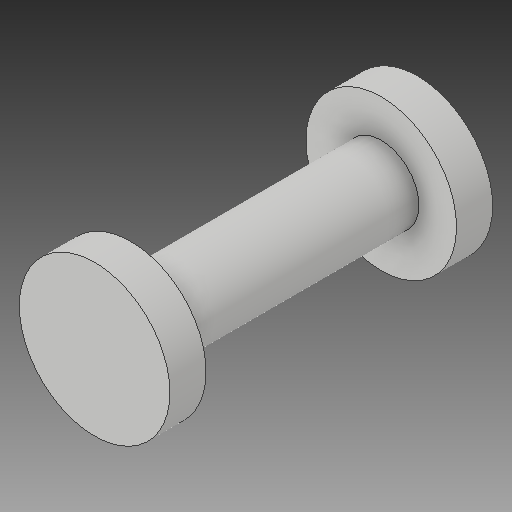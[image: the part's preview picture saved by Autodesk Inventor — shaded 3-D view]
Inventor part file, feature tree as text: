
AUTODESK INVENTOR PART (.ipt)
format: ipt  version: 2017 (Build 210142000, 142)  size: 111,104 bytes
history: native  units: in
note: dims shown in document units (in); Inventor stores cm internally (conversion verified against a paired STEP export)
features: extrude x3, sketch x3
ambient origin geometry x8: Origin, YZ Plane, XZ Plane, XY Plane, X Axis, Y Axis, Z Axis, Center Point
bodies: Solid1 (feature_tree)
feature tree (6):
  extrude  "Extrusion1"  Depth=0.416in TaperAngle=0.0deg
  extrude  "Extrusion2"  Depth=0.06in TaperAngle=0.0deg
  extrude  "Extrusion3"  [1 undecoded]
  sketch  "Sketch1"  dims[d0=0.125in d1=0.416in d2=0.0in]
  sketch  "Sketch2"  dims[d3=0.25in d4=0.06in d5=0.0in]
  sketch  "Sketch3"  dims[d6=0.06in d7=0.0in]
note: 1 required parameter value undecoded (feature->parameter linkage not recoverable at this tier; creation-order binding heuristic only, values carry confidence <= 0.55)
